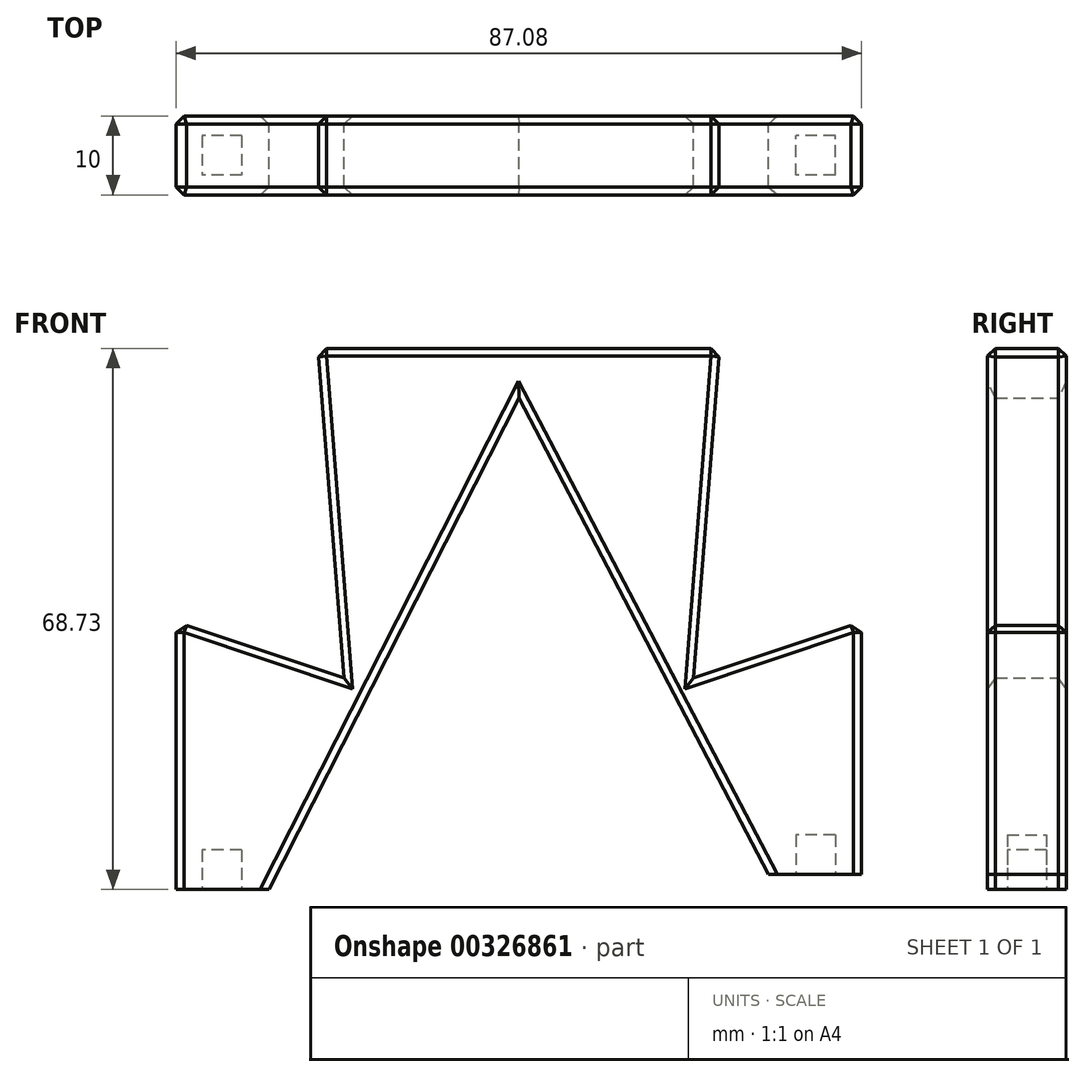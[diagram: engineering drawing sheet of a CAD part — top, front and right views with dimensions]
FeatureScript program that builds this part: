
annotation { "Feature Type Name" : "Feature", "Feature Type Description" : "" }
export const myFeature = defineFeature(function(context is Context, id is Id, definition is map)
    precondition{}
    {
        {
            var Q0;
            Q0=qCreatedBy(makeId("Front.planeOp"),FACE);
            var sketch = newSketch(context, id + "F0", { "sketchPlane" : qUnion([Q0])});
            skLineSegment(sketch, "E0", {"start": v(19.62, 0) * mm, "end": v(31.42, 0) * mm});
            skLineSegment(sketch, "E1", {"start": v(31.42, 0) * mm, "end": v(31.42, 32.1) * mm});
            skLineSegment(sketch, "E2", {"start": v(31.42, 32.1) * mm, "end": v(10.08, 24.96) * mm});
            skLineSegment(sketch, "E3", {"start": v(10.08, 24.96) * mm, "end": v(13.38, 66.83) * mm});
            skLineSegment(sketch, "E4", {"start": v(13.38, 66.83) * mm, "end": v(-37.62, 66.83) * mm});
            skLineSegment(sketch, "E5", {"start": v(-37.62, 66.83) * mm, "end": v(-34.33, 24.96) * mm});
            skLineSegment(sketch, "E6", {"start": v(-34.33, 24.96) * mm, "end": v(-55.66, 32.1) * mm});
            skLineSegment(sketch, "E7", {"start": v(-55.66, 32.1) * mm, "end": v(-55.66, -1.9) * mm});
            skLineSegment(sketch, "E8", {"start": v(-55.66, -1.9) * mm, "end": v(-43.86, -1.9) * mm});
            skLineSegment(sketch, "E9", {"start": v(-12.12, 66.83) * mm, "end": v(-12.12, 60.49) * mm});
            skPoint(sketch, "E9.endSnap0", {"position": v(-12.12, 66.83) * mm});
            skLineSegment(sketch, "E10", {"start": v(-12.12, 60.49) * mm, "end": v(-43.86, -1.9) * mm});
            skLineSegment(sketch, "E11", {"start": v(19.62, 0) * mm, "end": v(-12.12, 60.49) * mm});
            skSolve(sketch);
        }
        {
            var Q0;
            Q0=makeQuery(id+"F0.imprint","IMPRINT",FACE,{"disambiguationData":[TD([[makeQuery(id+"F0.imprint","IMPRINT",EDGE,{"derivedFrom":sQuery(id+"F0.wireOp",EDGE,"E0")}),1.0]])]});
            var Q1;
            {var subQ0=sQuery(id+"F0.wireOp",EDGE,"E5");Q1=makeQuery(id+"F0.imprint","IMPRINT",FACE,{"disambiguationData":[TD([[makeQuery(id+"F0.imprint","IMPRINT",EDGE,{"derivedFrom":subQ0}),1.0]])]});}
            extrude(context, id + "F1", {"entities" : qUnion([Q0, Q1]), "depth" : 10 * mm});
        }
        {
            var Q0;
            Q0=makeQuery(id+"F1.opExtrude","CAP_EDGE",EDGE,{"disambiguationData":[OSD([sQuery(id+"F0.wireOp",EDGE,"E3")])],"isStart":false});
            var Q1;
            Q1=makeQuery(id+"F1.opExtrude","CAP_EDGE",EDGE,{"disambiguationData":[OSD([sQuery(id+"F0.wireOp",EDGE,"E4")])],"isStart":false});
            var Q2;
            Q2=makeQuery(id+"F1.opExtrude","CAP_EDGE",EDGE,{"disambiguationData":[OSD([sQuery(id+"F0.wireOp",EDGE,"E5")])],"isStart":false});
            var Q3;
            Q3=makeQuery(id+"F1.opExtrude","CAP_EDGE",EDGE,{"disambiguationData":[OSD([sQuery(id+"F0.wireOp",EDGE,"E6")])],"isStart":false});
            var Q4;
            Q4=makeQuery(id+"F1.opExtrude","CAP_EDGE",EDGE,{"disambiguationData":[OSD([sQuery(id+"F0.wireOp",EDGE,"E7")])],"isStart":false});
            var Q5;
            Q5=makeQuery(id+"F1.opExtrude","CAP_EDGE",EDGE,{"disambiguationData":[OSD([sQuery(id+"F0.wireOp",EDGE,"E10")])],"isStart":false});
            var Q6;
            Q6=makeQuery(id+"F1.opExtrude","CAP_EDGE",EDGE,{"disambiguationData":[OSD([sQuery(id+"F0.wireOp",EDGE,"E2")])],"isStart":false});
            var Q7;
            Q7=makeQuery(id+"F1.opExtrude","CAP_EDGE",EDGE,{"disambiguationData":[OSD([sQuery(id+"F0.wireOp",EDGE,"E1")])],"isStart":false});
            var Q8;
            Q8=makeQuery(id+"F1.opExtrude","SWEPT_EDGE",EDGE,{"disambiguationData":[OSD([sQuery(id+"F0.wireOp",EDGE,"E3"),sQuery(id+"F0.wireOp",EDGE,"E4")])]});
            var Q9;
            Q9=makeQuery(id+"F1.opExtrude","SWEPT_EDGE",EDGE,{"disambiguationData":[OSD([sQuery(id+"F0.wireOp",EDGE,"E1"),sQuery(id+"F0.wireOp",EDGE,"E2")])]});
            var Q10;
            Q10=makeQuery(id+"F1.opExtrude","CAP_EDGE",EDGE,{"disambiguationData":[OSD([sQuery(id+"F0.wireOp",EDGE,"E2")])],"isStart":true});
            var Q11;
            Q11=makeQuery(id+"F1.opExtrude","CAP_EDGE",EDGE,{"disambiguationData":[OSD([sQuery(id+"F0.wireOp",EDGE,"E1")])],"isStart":true});
            var Q12;
            Q12=makeQuery(id+"F1.opExtrude","CAP_EDGE",EDGE,{"disambiguationData":[OSD([sQuery(id+"F0.wireOp",EDGE,"E11")])],"isStart":true});
            var Q13;
            Q13=makeQuery(id+"F1.opExtrude","CAP_EDGE",EDGE,{"disambiguationData":[OSD([sQuery(id+"F0.wireOp",EDGE,"E10")])],"isStart":true});
            var Q14;
            Q14=makeQuery(id+"F1.opExtrude","SWEPT_EDGE",EDGE,{"disambiguationData":[OSD([sQuery(id+"F0.wireOp",EDGE,"E6"),sQuery(id+"F0.wireOp",EDGE,"E7")])]});
            var Q15;
            Q15=makeQuery(id+"F1.opExtrude","CAP_EDGE",EDGE,{"disambiguationData":[OSD([sQuery(id+"F0.wireOp",EDGE,"E7")])],"isStart":true});
            var Q16;
            Q16=makeQuery(id+"F1.opExtrude","CAP_EDGE",EDGE,{"disambiguationData":[OSD([sQuery(id+"F0.wireOp",EDGE,"E6")])],"isStart":true});
            var Q17;
            Q17=makeQuery(id+"F1.opExtrude","CAP_EDGE",EDGE,{"disambiguationData":[OSD([sQuery(id+"F0.wireOp",EDGE,"E5")])],"isStart":true});
            var Q18;
            Q18=makeQuery(id+"F1.opExtrude","CAP_EDGE",EDGE,{"disambiguationData":[OSD([sQuery(id+"F0.wireOp",EDGE,"E3")])],"isStart":true});
            var Q19;
            Q19=makeQuery(id+"F1.opExtrude","CAP_EDGE",EDGE,{"disambiguationData":[OSD([sQuery(id+"F0.wireOp",EDGE,"E4")])],"isStart":true});
            var Q20;
            Q20=makeQuery(id+"F1.opExtrude","SWEPT_EDGE",EDGE,{"disambiguationData":[OSD([sQuery(id+"F0.wireOp",EDGE,"E4"),sQuery(id+"F0.wireOp",EDGE,"E5")])]});
            var Q21;
            Q21=makeQuery(id+"F1.opExtrude","CAP_EDGE",EDGE,{"disambiguationData":[OSD([sQuery(id+"F0.wireOp",EDGE,"E11")])],"isStart":false});
            chamfer(context, id + "F2", {"entities" : qUnion([Q0, Q1, Q2, Q3, Q4, Q5, Q6, Q7, Q8, Q9, Q10, Q11, Q12, Q13, Q14, Q15, Q16, Q17, Q18, Q19, Q20, Q21]), "width" : 1 * mm, "tangentPropagation" : true});
        }
        {
            var Q0;
            Q0=makeQuery(id+"F1.opExtrude","SWEPT_FACE",FACE,{"disambiguationData":[OSD([sQuery(id+"F0.wireOp",EDGE,"E0")])]});
            var sketch = newSketch(context, id + "F3", { "sketchPlane" : qUnion([Q0])});
            skLineSegment(sketch, "E12", {"start": v(25.59, 0) * mm, "end": v(25.59, 10) * mm});
            skLineSegment(sketch, "E13", {"start": v(19.62, 5) * mm, "end": v(31.42, 5) * mm});
            skPoint(sketch, "E14", {"position": v(25.59, 5) * mm});
            skLineSegment(sketch, "E15.bottom", {"start": v(28.09, 7.5) * mm, "end": v(23.09, 7.5) * mm});
            skLineSegment(sketch, "E15.top", {"start": v(28.09, 2.5) * mm, "end": v(23.09, 2.5) * mm});
            skLineSegment(sketch, "E15.left", {"start": v(28.09, 7.5) * mm, "end": v(28.09, 2.5) * mm});
            skLineSegment(sketch, "E15.right", {"start": v(23.09, 7.5) * mm, "end": v(23.09, 2.5) * mm});
            skSolve(sketch);
        }
        {
            var Q0;
            {var subQ0=sQuery(id+"F3.wireOp",EDGE,"E15.top");var subQ1=sQuery(id+"F3.wireOp",EDGE,"E12");var subQ2=makeQuery(id+"F3.imprint","INTERSECT",VERTEX,{"derivedFrom":[subQ1,subQ0]});Q0=makeQuery(id+"F3.imprint","IMPRINT",FACE,{"disambiguationData":[TD([[makeQuery(id+"F3.imprint","IMPRINT",EDGE,{"disambiguationData":[TD([[subQ2,-1.0]])],"derivedFrom":subQ1}),-1.0]])]});}
            var Q1;
            {var subQ0=sQuery(id+"F3.wireOp",EDGE,"E15.top");var subQ1=sQuery(id+"F3.wireOp",EDGE,"E12");var subQ2=makeQuery(id+"F3.imprint","INTERSECT",VERTEX,{"derivedFrom":[subQ1,subQ0]});Q1=makeQuery(id+"F3.imprint","IMPRINT",FACE,{"disambiguationData":[TD([[makeQuery(id+"F3.imprint","IMPRINT",EDGE,{"disambiguationData":[TD([[subQ2,-1.0]])],"derivedFrom":subQ1}),1.0]])]});}
            var Q2;
            {var subQ0=sQuery(id+"F3.wireOp",EDGE,"E13");var subQ1=sQuery(id+"F3.wireOp",EDGE,"E12");var subQ2=makeQuery(id+"F3.imprint","INTERSECT",VERTEX,{"derivedFrom":[subQ1,subQ0]});Q2=makeQuery(id+"F3.imprint","IMPRINT",FACE,{"disambiguationData":[TD([[makeQuery(id+"F3.imprint","IMPRINT",EDGE,{"disambiguationData":[TD([[subQ2,-1.0]])],"derivedFrom":subQ1}),1.0]])]});}
            var Q3;
            {var subQ0=sQuery(id+"F3.wireOp",EDGE,"E13");var subQ1=sQuery(id+"F3.wireOp",EDGE,"E12");var subQ2=makeQuery(id+"F3.imprint","INTERSECT",VERTEX,{"derivedFrom":[subQ1,subQ0]});Q3=makeQuery(id+"F3.imprint","IMPRINT",FACE,{"disambiguationData":[TD([[makeQuery(id+"F3.imprint","IMPRINT",EDGE,{"disambiguationData":[TD([[subQ2,-1.0]])],"derivedFrom":subQ1}),-1.0]])]});}
            extrude(context, id + "F4", {"entities" : qUnion([Q0, Q1, Q2, Q3]), "operationType" : NewBodyOperationType.REMOVE, "oppositeDirection" : true, "depth" : 5 * mm});
        }
        {
            var Q0;
            Q0=makeQuery(id+"F1.opExtrude","SWEPT_FACE",FACE,{"disambiguationData":[OSD([sQuery(id+"F0.wireOp",EDGE,"E8")])]});
            var sketch = newSketch(context, id + "F5", { "sketchPlane" : qUnion([Q0])});
            skLineSegment(sketch, "E16", {"start": v(-55.66, 5) * mm, "end": v(-43.86, 5) * mm});
            skLineSegment(sketch, "E17", {"start": v(-49.82, 0) * mm, "end": v(-49.82, 10) * mm});
            skPoint(sketch, "E18", {"position": v(-49.82, 5) * mm});
            skLineSegment(sketch, "E19.bottom", {"start": v(-47.32, 2.5) * mm, "end": v(-52.32, 2.5) * mm});
            skLineSegment(sketch, "E19.top", {"start": v(-47.32, 7.5) * mm, "end": v(-52.32, 7.5) * mm});
            skLineSegment(sketch, "E19.left", {"start": v(-47.32, 2.5) * mm, "end": v(-47.32, 7.5) * mm});
            skLineSegment(sketch, "E19.right", {"start": v(-52.32, 2.5) * mm, "end": v(-52.32, 7.5) * mm});
            skSolve(sketch);
        }
        {
            var Q0;
            {var subQ0=sQuery(id+"F5.wireOp",EDGE,"E19.right");var subQ1=sQuery(id+"F5.wireOp",EDGE,"E16");var subQ2=makeQuery(id+"F5.imprint","INTERSECT",VERTEX,{"derivedFrom":[subQ1,subQ0]});Q0=makeQuery(id+"F5.imprint","IMPRINT",FACE,{"disambiguationData":[TD([[makeQuery(id+"F5.imprint","IMPRINT",EDGE,{"disambiguationData":[TD([[subQ2,-1.0]])],"derivedFrom":subQ1}),1.0]])]});}
            var Q1;
            {var subQ0=sQuery(id+"F5.wireOp",EDGE,"E19.right");var subQ1=sQuery(id+"F5.wireOp",EDGE,"E16");var subQ2=makeQuery(id+"F5.imprint","INTERSECT",VERTEX,{"derivedFrom":[subQ1,subQ0]});Q1=makeQuery(id+"F5.imprint","IMPRINT",FACE,{"disambiguationData":[TD([[makeQuery(id+"F5.imprint","IMPRINT",EDGE,{"disambiguationData":[TD([[subQ2,-1.0]])],"derivedFrom":subQ1}),-1.0]])]});}
            var Q2;
            {var subQ0=sQuery(id+"F5.wireOp",EDGE,"E17");var subQ1=sQuery(id+"F5.wireOp",EDGE,"E16");var subQ2=makeQuery(id+"F5.imprint","INTERSECT",VERTEX,{"derivedFrom":[subQ1,subQ0]});Q2=makeQuery(id+"F5.imprint","IMPRINT",FACE,{"disambiguationData":[TD([[makeQuery(id+"F5.imprint","IMPRINT",EDGE,{"disambiguationData":[TD([[subQ2,-1.0]])],"derivedFrom":subQ1}),-1.0]])]});}
            var Q3;
            {var subQ0=sQuery(id+"F5.wireOp",EDGE,"E17");var subQ1=sQuery(id+"F5.wireOp",EDGE,"E16");var subQ2=makeQuery(id+"F5.imprint","INTERSECT",VERTEX,{"derivedFrom":[subQ1,subQ0]});Q3=makeQuery(id+"F5.imprint","IMPRINT",FACE,{"disambiguationData":[TD([[makeQuery(id+"F5.imprint","IMPRINT",EDGE,{"disambiguationData":[TD([[subQ2,-1.0]])],"derivedFrom":subQ1}),1.0]])]});}
            extrude(context, id + "F6", {"entities" : qUnion([Q0, Q1, Q2, Q3]), "operationType" : NewBodyOperationType.REMOVE, "oppositeDirection" : true, "depth" : 5 * mm});
        }
    });
